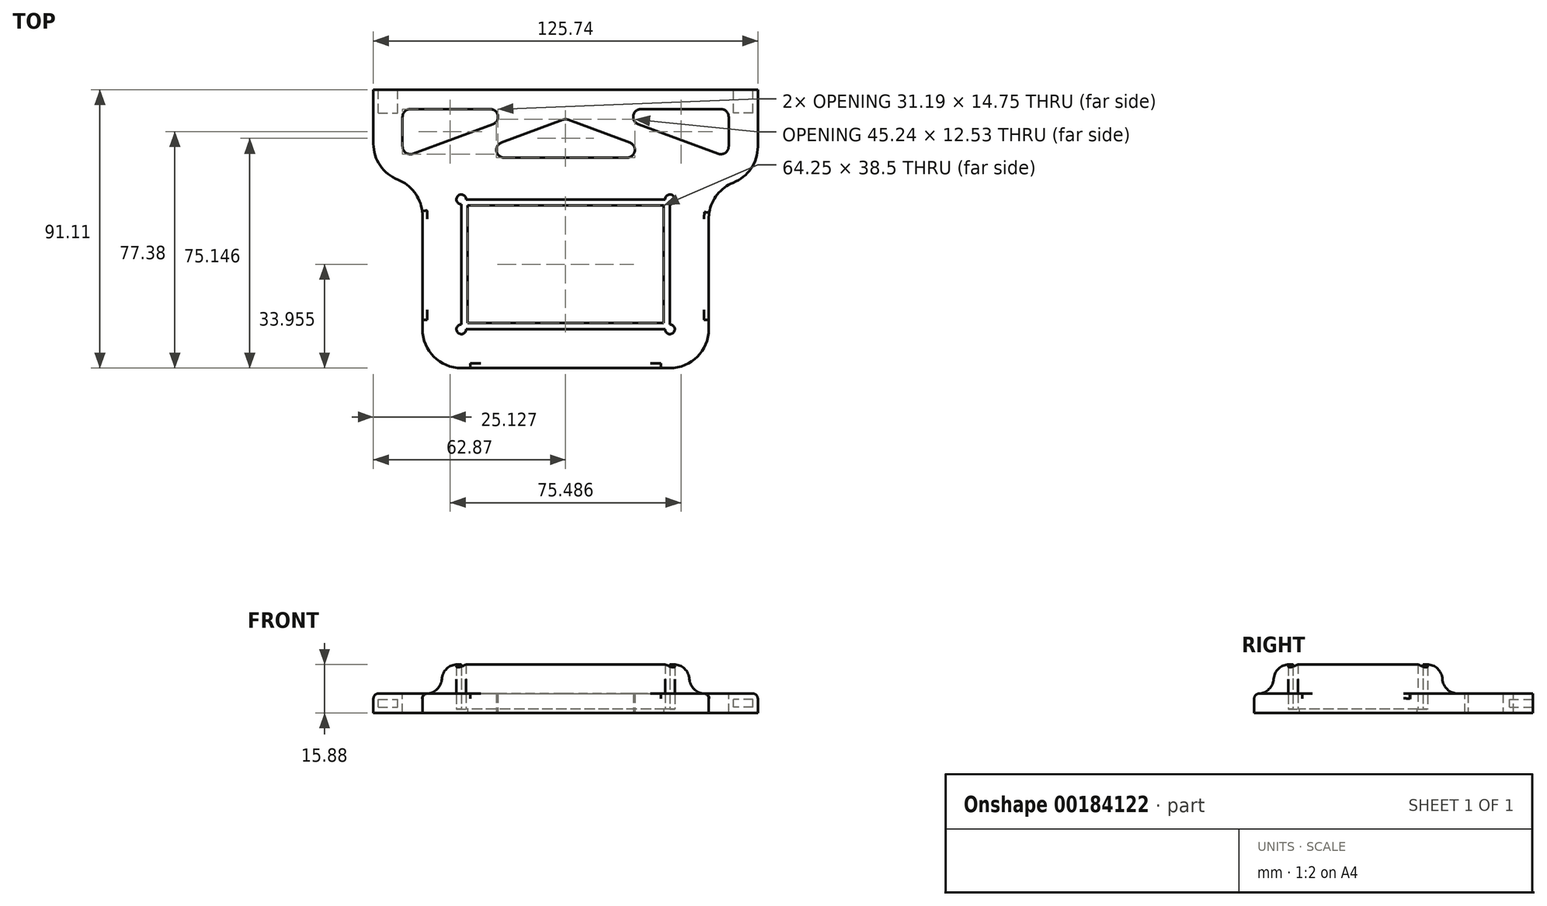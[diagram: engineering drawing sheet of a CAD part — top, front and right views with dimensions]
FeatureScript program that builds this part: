
annotation { "Feature Type Name" : "Feature", "Feature Type Description" : "" }
export const myFeature = defineFeature(function(context is Context, id is Id, definition is map)
    precondition{}
    {
        {
            var Q0;
            Q0=qCreatedBy(makeId("Top.planeOp"),FACE);
            var sketch = newSketch(context, id + "F0", { "sketchPlane" : qUnion([Q0])});
            skLineSegment(sketch, "E0", {"start": v(-53.34, 0) * mm, "end": v(-53.34, 47.62) * mm});
            skLineSegment(sketch, "E1", {"start": v(53.34, 0) * mm, "end": v(53.34, 47.62) * mm});
            skLineSegment(sketch, "E2", {"start": v(-39.21, 76.2) * mm, "end": v(39.21, 76.2) * mm});
            skArc(sketch, "E3", {"start": v(-39.21, 76.2) * mm, "mid": v(-55.15, 66.3) * mm, "end": v(-53.34, 47.62) * mm});
            skArc(sketch, "E4", {"start": v(53.34, 47.62) * mm, "mid": v(55.15, 66.3) * mm, "end": v(39.21, 76.2) * mm});
            skPoint(sketch, "E5", {"position": v(0, 76.2) * mm});
            skLineSegment(sketch, "E6.bottom", {"start": v(-58.42, 0) * mm, "end": v(58.42, 0) * mm, "construction": true});
            skLineSegment(sketch, "E6.top", {"start": v(-58.42, -82.55) * mm, "end": v(58.42, -82.55) * mm, "construction": true});
            skLineSegment(sketch, "E6.left", {"start": v(-58.42, 0) * mm, "end": v(-58.42, -82.55) * mm, "construction": true});
            skLineSegment(sketch, "E6.right", {"start": v(58.42, 0) * mm, "end": v(58.42, -82.55) * mm, "construction": true});
            skLineSegment(sketch, "E7.bottom", {"start": v(34.12, -20.03) * mm, "end": v(-34.12, -20.03) * mm});
            skLineSegment(sketch, "E7.top", {"start": v(34.13, -62.53) * mm, "end": v(-34.12, -62.53) * mm});
            skLineSegment(sketch, "E7.left", {"start": v(34.12, -20.03) * mm, "end": v(34.12, -62.52) * mm});
            skLineSegment(sketch, "E7.right", {"start": v(-34.12, -20.02) * mm, "end": v(-34.12, -62.53) * mm});
            skPoint(sketch, "E7.middle", {"position": v(0, -41.27) * mm});
            skPoint(sketch, "E8", {"position": v(58.42, -41.27) * mm});
            skCircle(sketch, "E9", {"center": v(-34.12, -20.02) * mm, "radius": 1.59 * mm});
            skCircle(sketch, "E10", {"center": v(34.13, -20.03) * mm, "radius": 1.59 * mm});
            skCircle(sketch, "E11", {"center": v(34.13, -62.52) * mm, "radius": 1.59 * mm});
            skCircle(sketch, "E12", {"center": v(-34.12, -62.53) * mm, "radius": 1.59 * mm});
            skLineSegment(sketch, "E13.0", {"start": v(-62.87, 0) * mm, "end": v(-62.87, 44.78) * mm});
            skLineSegment(sketch, "E13.1", {"start": v(62.87, 0) * mm, "end": v(62.87, 44.78) * mm});
            skArc(sketch, "E13.2", {"start": v(62.87, 44.78) * mm, "mid": v(62.86, 72.08) * mm, "end": v(39.21, 85.72) * mm});
            skLineSegment(sketch, "E13.3", {"start": v(-39.21, 85.73) * mm, "end": v(39.21, 85.73) * mm});
            skArc(sketch, "E13.4", {"start": v(-39.21, 85.72) * mm, "mid": v(-62.86, 72.08) * mm, "end": v(-62.87, 44.78) * mm});
            skLineSegment(sketch, "E14", {"start": v(-62.87, 0) * mm, "end": v(-53.34, 0) * mm});
            skLineSegment(sketch, "E15", {"start": v(53.34, 0) * mm, "end": v(62.87, 0) * mm});
            skLineSegment(sketch, "E16", {"start": v(-53.34, 15.88) * mm, "end": v(53.34, 15.88) * mm});
            skLineSegment(sketch, "E17", {"start": v(62.87, 0) * mm, "end": v(62.87, -91.27) * mm});
            skLineSegment(sketch, "E18", {"start": v(62.86, -91.27) * mm, "end": v(-62.86, -91.27) * mm});
            skLineSegment(sketch, "E19", {"start": v(-62.87, -91.27) * mm, "end": v(-62.87, 0) * mm});
            skLineSegment(sketch, "E20", {"start": v(0, -91.27) * mm, "end": v(0, -62.53) * mm, "construction": true});
            skLineSegment(sketch, "E21", {"start": v(34.12, -41.28) * mm, "end": v(62.87, -41.28) * mm, "construction": true});
            skLineSegment(sketch, "E22.bottom", {"start": v(40.48, -13.67) * mm, "end": v(-40.48, -13.67) * mm});
            skLineSegment(sketch, "E22.top", {"start": v(40.48, -68.88) * mm, "end": v(-40.48, -68.88) * mm});
            skLineSegment(sketch, "E22.left", {"start": v(40.48, -13.67) * mm, "end": v(40.48, -68.88) * mm});
            skLineSegment(sketch, "E22.right", {"start": v(-40.48, -13.67) * mm, "end": v(-40.48, -68.88) * mm});
            skLineSegment(sketch, "E23", {"start": v(-62.87, 0) * mm, "end": v(-62.87, -12.7) * mm});
            skLineSegment(sketch, "E24", {"start": v(-62.87, -12.7) * mm, "end": v(-46.83, -12.7) * mm});
            skLineSegment(sketch, "E25", {"start": v(-46.83, -12.7) * mm, "end": v(-46.83, -75.22) * mm});
            skLineSegment(sketch, "E26", {"start": v(-46.83, -75.22) * mm, "end": v(46.83, -75.22) * mm});
            skLineSegment(sketch, "E27", {"start": v(46.83, -75.22) * mm, "end": v(46.83, -13.67) * mm});
            skLineSegment(sketch, "E28", {"start": v(46.83, -13.67) * mm, "end": v(62.87, -13.67) * mm});
            skLineSegment(sketch, "E29", {"start": v(62.87, -13.67) * mm, "end": v(62.87, 0) * mm});
            skLineSegment(sketch, "E30", {"start": v(-53.34, 15.88) * mm, "end": v(-62.87, 15.88) * mm});
            skLineSegment(sketch, "E31", {"start": v(53.34, 15.88) * mm, "end": v(62.87, 15.88) * mm});
            skSolve(sketch);
        }
        {
            var Q0;
            {var subQ16=sQuery(id+"F0.wireOp",EDGE,"E14");Q0=makeQuery(id+"F0.imprint","IMPRINT",FACE,{"disambiguationData":[TD([[makeQuery(id+"F0.imprint","IMPRINT",EDGE,{"derivedFrom":subQ16}),-1.0]])]});}
            var Q1;
            Q1=makeQuery(id+"F0.imprint","IMPRINT",FACE,{"disambiguationData":[TD([[makeQuery(id+"F0.imprint","IMPRINT",EDGE,{"derivedFrom":sQuery(id+"F0.wireOp",EDGE,"E22.bottom")}),1.0]])]});
            var Q2;
            {var subQ0=sQuery(id+"F0.wireOp",EDGE,"E14");Q2=makeQuery(id+"F0.imprint","IMPRINT",FACE,{"disambiguationData":[TD([[makeQuery(id+"F0.imprint","IMPRINT",EDGE,{"derivedFrom":subQ0}),1.0]])]});}
            var Q3;
            {var subQ0=sQuery(id+"F0.wireOp",EDGE,"E15");Q3=makeQuery(id+"F0.imprint","IMPRINT",FACE,{"disambiguationData":[TD([[makeQuery(id+"F0.imprint","IMPRINT",EDGE,{"derivedFrom":subQ0}),1.0]])]});}
            extrude(context, id + "F1", {"entities" : qUnion([Q0, Q1, Q2, Q3]), "depth" : 6.35 * mm});
        }
        {
            var Q0;
            Q0=makeQuery(id+"F0.imprint","IMPRINT",FACE,{"disambiguationData":[TD([[makeQuery(id+"F0.imprint","IMPRINT",EDGE,{"derivedFrom":sQuery(id+"F0.wireOp",EDGE,"E22.bottom")}),1.0]])]});
            extrude(context, id + "F2", {"entities" : qUnion([Q0]), "operationType" : NewBodyOperationType.ADD, "depth" : 15.88 * mm});
        }
        {
            var Q0;
            Q0=makeQuery(id+"F1.opExtrude","CAP_FACE",FACE,{"disambiguationData":[OSD([sQuery(id+"F0.wireOp",EDGE,"E7.bottom"),sQuery(id+"F0.wireOp",EDGE,"E7.top"),sQuery(id+"F0.wireOp",EDGE,"E7.left"),sQuery(id+"F0.wireOp",EDGE,"E7.right"),sQuery(id+"F0.wireOp",EDGE,"E9"),sQuery(id+"F0.wireOp",EDGE,"E10"),sQuery(id+"F0.wireOp",EDGE,"E11"),sQuery(id+"F0.wireOp",EDGE,"E12"),sQuery(id+"F0.wireOp",EDGE,"E13.0"),sQuery(id+"F0.wireOp",EDGE,"E13.1"),sQuery(id+"F0.wireOp",EDGE,"E16"),sQuery(id+"F0.wireOp",EDGE,"E23"),sQuery(id+"F0.wireOp",EDGE,"E24"),sQuery(id+"F0.wireOp",EDGE,"E25"),sQuery(id+"F0.wireOp",EDGE,"E26"),sQuery(id+"F0.wireOp",EDGE,"E27"),sQuery(id+"F0.wireOp",EDGE,"E28"),sQuery(id+"F0.wireOp",EDGE,"E29"),sQuery(id+"F0.wireOp",EDGE,"E30"),sQuery(id+"F0.wireOp",EDGE,"E31")])],"isStart":false});
            var sketch = newSketch(context, id + "F3", { "sketchPlane" : qUnion([Q0])});
            skLineSegment(sketch, "E32", {"start": v(-53.34, 9.52) * mm, "end": v(-53.34, -6.35) * mm});
            skLineSegment(sketch, "E33", {"start": v(-53.34, -6.35) * mm, "end": v(-10.48, 9.53) * mm});
            skLineSegment(sketch, "E34", {"start": v(-10.48, 9.53) * mm, "end": v(-53.34, 9.52) * mm});
            skLineSegment(sketch, "E35", {"start": v(10.48, 9.53) * mm, "end": v(53.34, 9.53) * mm});
            skLineSegment(sketch, "E36", {"start": v(53.34, 9.52) * mm, "end": v(53.34, -6.35) * mm});
            skLineSegment(sketch, "E37", {"start": v(53.34, -6.35) * mm, "end": v(10.48, 9.53) * mm});
            skLineSegment(sketch, "E38", {"start": v(0, 6.35) * mm, "end": v(-34.3, -6.35) * mm});
            skLineSegment(sketch, "E39", {"start": v(-34.3, -6.35) * mm, "end": v(34.3, -6.35) * mm});
            skLineSegment(sketch, "E40", {"start": v(34.3, -6.35) * mm, "end": v(0, 6.35) * mm});
            skLineSegment(sketch, "E41", {"start": v(-10.48, 9.53) * mm, "end": v(10.48, 9.53) * mm, "construction": true});
            skPoint(sketch, "E42", {"position": v(0, 9.53) * mm});
            skPoint(sketch, "E43", {"position": v(-53.34, 1.59) * mm});
            skPoint(sketch, "E44", {"position": v(-62.87, 1.59) * mm});
            skSolve(sketch);
        }
        {
            var Q0;
            Q0 = qSketchRegion(id + "F3", true);
            extrude(context, id + "F4", {"entities" : qUnion([Q0]), "operationType" : NewBodyOperationType.REMOVE, "endBound" : BoundingType.THROUGH_ALL, "oppositeDirection" : true, "depth" : 25.4 * mm});
        }
        {
            var Q0;
            Q0=makeQuery(id+"F1.opExtrude","SWEPT_EDGE",EDGE,{"disambiguationData":[OSD([sQuery(id+"F0.wireOp",EDGE,"E25"),sQuery(id+"F0.wireOp",EDGE,"E26")])]});
            var Q1;
            Q1=makeQuery(id+"F1.opExtrude","SWEPT_EDGE",EDGE,{"disambiguationData":[OSD([sQuery(id+"F0.wireOp",EDGE,"E26"),sQuery(id+"F0.wireOp",EDGE,"E27")])]});
            var Q2;
            Q2=makeQuery(id+"F1.opExtrude","SWEPT_EDGE",EDGE,{"disambiguationData":[OSD([sQuery(id+"F0.wireOp",EDGE,"E24"),sQuery(id+"F0.wireOp",EDGE,"E25")])]});
            var Q3;
            Q3=makeQuery(id+"F1.opExtrude","SWEPT_EDGE",EDGE,{"disambiguationData":[OSD([sQuery(id+"F0.wireOp",EDGE,"E27"),sQuery(id+"F0.wireOp",EDGE,"E28")])]});
            var Q4;
            Q4=makeQuery(id+"F2.opExtrude","SWEPT_EDGE",EDGE,{"disambiguationData":[OSD([sQuery(id+"F0.wireOp",EDGE,"E22.top"),sQuery(id+"F0.wireOp",EDGE,"E22.left")])]});
            var Q5;
            Q5=makeQuery(id+"F2.opExtrude","SWEPT_EDGE",EDGE,{"disambiguationData":[OSD([sQuery(id+"F0.wireOp",EDGE,"E22.top"),sQuery(id+"F0.wireOp",EDGE,"E22.right")])]});
            var Q6;
            Q6=makeQuery(id+"F2.opExtrude","SWEPT_EDGE",EDGE,{"disambiguationData":[OSD([sQuery(id+"F0.wireOp",EDGE,"E22.bottom"),sQuery(id+"F0.wireOp",EDGE,"E22.left")])]});
            var Q7;
            Q7=makeQuery(id+"F2.opExtrude","SWEPT_EDGE",EDGE,{"disambiguationData":[OSD([sQuery(id+"F0.wireOp",EDGE,"E22.bottom"),sQuery(id+"F0.wireOp",EDGE,"E22.right")])]});
            fillet(context, id + "F5", {"entities" : qUnion([Q0, Q1, Q2, Q3, Q4, Q5, Q6, Q7]), "radius" : 12.7 * mm, "tangentPropagation" : true, "allowEdgeOverflow" : false});
        }
        {
            var Q0;
            Q0=makeQuery(id+"F1.opExtrude","SWEPT_EDGE",EDGE,{"disambiguationData":[OSD([sQuery(id+"F0.wireOp",EDGE,"E19"),sQuery(id+"F0.wireOp",EDGE,"E23"),sQuery(id+"F0.wireOp",EDGE,"E24")])]});
            var Q1;
            Q1=makeQuery(id+"F1.opExtrude","SWEPT_EDGE",EDGE,{"disambiguationData":[OSD([sQuery(id+"F0.wireOp",EDGE,"E17"),sQuery(id+"F0.wireOp",EDGE,"E28"),sQuery(id+"F0.wireOp",EDGE,"E29")])]});
            fillet(context, id + "F6", {"entities" : qUnion([Q0, Q1]), "radius" : 12.7 * mm, "tangentPropagation" : true, "allowEdgeOverflow" : false});
        }
        {
            var Q0;
            Q0=makeQuery(id+"F5.opFillet","BLEND_EDGE",EDGE,{"blendedFrom":[makeQuery(id+"F2.opExtrude","SWEPT_EDGE",EDGE,{"disambiguationData":[OSD([sQuery(id+"F0.wireOp",EDGE,"E22.bottom"),sQuery(id+"F0.wireOp",EDGE,"E22.left")])]}),makeQuery(id+"F1.opExtrude","CAP_FACE",FACE,{"disambiguationData":[OSD([sQuery(id+"F0.wireOp",EDGE,"E7.bottom"),sQuery(id+"F0.wireOp",EDGE,"E7.top"),sQuery(id+"F0.wireOp",EDGE,"E7.left"),sQuery(id+"F0.wireOp",EDGE,"E7.right"),sQuery(id+"F0.wireOp",EDGE,"E9"),sQuery(id+"F0.wireOp",EDGE,"E10"),sQuery(id+"F0.wireOp",EDGE,"E11"),sQuery(id+"F0.wireOp",EDGE,"E12"),sQuery(id+"F0.wireOp",EDGE,"E13.0"),sQuery(id+"F0.wireOp",EDGE,"E13.1"),sQuery(id+"F0.wireOp",EDGE,"E16"),sQuery(id+"F0.wireOp",EDGE,"E23"),sQuery(id+"F0.wireOp",EDGE,"E24"),sQuery(id+"F0.wireOp",EDGE,"E25"),sQuery(id+"F0.wireOp",EDGE,"E26"),sQuery(id+"F0.wireOp",EDGE,"E27"),sQuery(id+"F0.wireOp",EDGE,"E28"),sQuery(id+"F0.wireOp",EDGE,"E29"),sQuery(id+"F0.wireOp",EDGE,"E30"),sQuery(id+"F0.wireOp",EDGE,"E31")])],"isStart":false})],"blendedInto":[makeQuery(id+"F1.opExtrude","CAP_FACE",FACE,{"disambiguationData":[OSD([sQuery(id+"F0.wireOp",EDGE,"E7.bottom"),sQuery(id+"F0.wireOp",EDGE,"E7.top"),sQuery(id+"F0.wireOp",EDGE,"E7.left"),sQuery(id+"F0.wireOp",EDGE,"E7.right"),sQuery(id+"F0.wireOp",EDGE,"E9"),sQuery(id+"F0.wireOp",EDGE,"E10"),sQuery(id+"F0.wireOp",EDGE,"E11"),sQuery(id+"F0.wireOp",EDGE,"E12"),sQuery(id+"F0.wireOp",EDGE,"E13.0"),sQuery(id+"F0.wireOp",EDGE,"E13.1"),sQuery(id+"F0.wireOp",EDGE,"E16"),sQuery(id+"F0.wireOp",EDGE,"E23"),sQuery(id+"F0.wireOp",EDGE,"E24"),sQuery(id+"F0.wireOp",EDGE,"E25"),sQuery(id+"F0.wireOp",EDGE,"E26"),sQuery(id+"F0.wireOp",EDGE,"E27"),sQuery(id+"F0.wireOp",EDGE,"E28"),sQuery(id+"F0.wireOp",EDGE,"E29"),sQuery(id+"F0.wireOp",EDGE,"E30"),sQuery(id+"F0.wireOp",EDGE,"E31")])],"isStart":false})]});
            fillet(context, id + "F7", {"entities" : qUnion([Q0]), "radius" : 5.08 * mm, "tangentPropagation" : true, "allowEdgeOverflow" : false});
        }
        {
            var Q0;
            Q0=makeQuery(id+"F4.boolean.opBoolean","COPY",EDGE,{"derivedFrom":makeQuery(id+"F4.opExtrude","SWEPT_EDGE",EDGE,{"disambiguationData":[OSD([sQuery(id+"F3.wireOp",EDGE,"E32"),sQuery(id+"F3.wireOp",EDGE,"E34")])]})});
            var Q1;
            Q1=makeQuery(id+"F4.boolean.opBoolean","COPY",EDGE,{"derivedFrom":makeQuery(id+"F4.opExtrude","SWEPT_EDGE",EDGE,{"disambiguationData":[OSD([sQuery(id+"F3.wireOp",EDGE,"E32"),sQuery(id+"F3.wireOp",EDGE,"E33")])]})});
            var Q2;
            Q2=makeQuery(id+"F4.boolean.opBoolean","COPY",EDGE,{"derivedFrom":makeQuery(id+"F4.opExtrude","SWEPT_EDGE",EDGE,{"disambiguationData":[OSD([sQuery(id+"F3.wireOp",EDGE,"E36"),sQuery(id+"F3.wireOp",EDGE,"E37")])]})});
            var Q3;
            Q3=makeQuery(id+"F4.boolean.opBoolean","COPY",EDGE,{"derivedFrom":makeQuery(id+"F4.opExtrude","SWEPT_EDGE",EDGE,{"disambiguationData":[OSD([sQuery(id+"F3.wireOp",EDGE,"E35"),sQuery(id+"F3.wireOp",EDGE,"E37")])]})});
            var Q4;
            Q4=makeQuery(id+"F4.boolean.opBoolean","COPY",EDGE,{"derivedFrom":makeQuery(id+"F4.opExtrude","SWEPT_EDGE",EDGE,{"disambiguationData":[OSD([sQuery(id+"F3.wireOp",EDGE,"E38"),sQuery(id+"F3.wireOp",EDGE,"E40")])]})});
            var Q5;
            Q5=makeQuery(id+"F4.boolean.opBoolean","COPY",EDGE,{"derivedFrom":makeQuery(id+"F4.opExtrude","SWEPT_EDGE",EDGE,{"disambiguationData":[OSD([sQuery(id+"F3.wireOp",EDGE,"E39"),sQuery(id+"F3.wireOp",EDGE,"E40")])]})});
            var Q6;
            Q6=makeQuery(id+"F4.boolean.opBoolean","COPY",EDGE,{"derivedFrom":makeQuery(id+"F4.opExtrude","SWEPT_EDGE",EDGE,{"disambiguationData":[OSD([sQuery(id+"F3.wireOp",EDGE,"E38"),sQuery(id+"F3.wireOp",EDGE,"E39")])]})});
            var Q7;
            Q7=makeQuery(id+"F4.boolean.opBoolean","COPY",EDGE,{"derivedFrom":makeQuery(id+"F4.opExtrude","SWEPT_EDGE",EDGE,{"disambiguationData":[OSD([sQuery(id+"F3.wireOp",EDGE,"E33"),sQuery(id+"F3.wireOp",EDGE,"E34")])]})});
            var Q8;
            Q8=makeQuery(id+"F4.boolean.opBoolean","COPY",EDGE,{"derivedFrom":makeQuery(id+"F4.opExtrude","SWEPT_EDGE",EDGE,{"disambiguationData":[OSD([sQuery(id+"F3.wireOp",EDGE,"E35"),sQuery(id+"F3.wireOp",EDGE,"E36")])]})});
            fillet(context, id + "F8", {"entities" : qUnion([Q0, Q1, Q2, Q3, Q4, Q5, Q6, Q7, Q8]), "radius" : 2.54 * mm, "tangentPropagation" : true, "allowEdgeOverflow" : false});
        }
        {
            var Q0;
            Q0=makeQuery(id+"F1.opExtrude","SWEPT_FACE",FACE,{"disambiguationData":[OSD([sQuery(id+"F0.wireOp",EDGE,"E16"),sQuery(id+"F0.wireOp",EDGE,"E30"),sQuery(id+"F0.wireOp",EDGE,"E31")])]});
            var sketch = newSketch(context, id + "F9", { "sketchPlane" : qUnion([Q0])});
            skLineSegment(sketch, "E45.bottom", {"start": v(61.28, 1.9) * mm, "end": v(54.93, 1.9) * mm});
            skLineSegment(sketch, "E45.top", {"start": v(61.28, 4.44) * mm, "end": v(54.93, 4.44) * mm});
            skLineSegment(sketch, "E45.left", {"start": v(61.28, 1.9) * mm, "end": v(61.28, 4.44) * mm});
            skLineSegment(sketch, "E45.right", {"start": v(54.93, 1.9) * mm, "end": v(54.93, 4.44) * mm});
            skPoint(sketch, "E45.middle", {"position": v(58.1, 3.17) * mm});
            skLineSegment(sketch, "E46.bottom", {"start": v(-61.28, 1.9) * mm, "end": v(-54.93, 1.9) * mm});
            skLineSegment(sketch, "E46.top", {"start": v(-61.28, 4.44) * mm, "end": v(-54.93, 4.44) * mm});
            skLineSegment(sketch, "E46.left", {"start": v(-61.28, 1.9) * mm, "end": v(-61.28, 4.44) * mm});
            skLineSegment(sketch, "E46.right", {"start": v(-54.93, 1.9) * mm, "end": v(-54.93, 4.44) * mm});
            skPoint(sketch, "E46.middle", {"position": v(-58.1, 3.17) * mm});
            skLineSegment(sketch, "E47", {"start": v(0, 0) * mm, "end": v(0, 6.35) * mm, "construction": true});
            skPoint(sketch, "E48", {"position": v(0, 3.17) * mm});
            skLineSegment(sketch, "E49", {"start": v(-58.1, 3.17) * mm, "end": v(58.1, 3.18) * mm, "construction": true});
            skLineSegment(sketch, "E50", {"start": v(-62.87, 6.35) * mm, "end": v(-62.87, 3.17) * mm, "construction": true});
            skLineSegment(sketch, "E51", {"start": v(-62.87, 3.17) * mm, "end": v(-62.87, 0) * mm, "construction": true});
            skSolve(sketch);
        }
        {
            var Q0;
            Q0 = qSketchRegion(id + "F9", true);
            extrude(context, id + "F10", {"entities" : qUnion([Q0]), "operationType" : NewBodyOperationType.REMOVE, "oppositeDirection" : true, "depth" : 7.62 * mm});
        }
        {
            var Q0;
            {var subQ1=sQuery(id+"F0.wireOp",EDGE,"E14");Q0=makeQuery(id+"F0.imprint","IMPRINT",FACE,{"disambiguationData":[TD([[makeQuery(id+"F0.imprint","IMPRINT",EDGE,{"derivedFrom":subQ1}),-1.0]])]});}
            var sketch = newSketch(context, id + "F11", { "sketchPlane" : qUnion([Q0])});
            skLineSegment(sketch, "E52.bottom", {"start": v(32.13, -22.03) * mm, "end": v(-32.12, -22.03) * mm});
            skLineSegment(sketch, "E52.top", {"start": v(32.13, -60.53) * mm, "end": v(-32.12, -60.53) * mm});
            skLineSegment(sketch, "E52.left", {"start": v(32.13, -22.03) * mm, "end": v(32.13, -60.53) * mm});
            skLineSegment(sketch, "E52.right", {"start": v(-32.12, -22.03) * mm, "end": v(-32.12, -60.53) * mm});
            skPoint(sketch, "E52.middle", {"position": v(0, -41.28) * mm});
            skLineSegment(sketch, "E53.bottom", {"start": v(35.71, -18.44) * mm, "end": v(-35.71, -18.44) * mm});
            skLineSegment(sketch, "E53.top", {"start": v(35.71, -64.11) * mm, "end": v(-35.71, -64.11) * mm});
            skLineSegment(sketch, "E53.left", {"start": v(35.71, -18.44) * mm, "end": v(35.71, -64.11) * mm});
            skLineSegment(sketch, "E53.right", {"start": v(-35.71, -18.44) * mm, "end": v(-35.71, -64.11) * mm});
            skSolve(sketch);
        }
        {
            var Q0;
            Q0=makeQuery(id+"F0.imprint","IMPRINT",FACE,{"disambiguationData":[TD([[makeQuery(id+"F0.imprint","IMPRINT",EDGE,{"derivedFrom":sQuery(id+"F0.wireOp",EDGE,"E22.bottom")}),1.0]])]});
            var Q1;
            Q1=makeQuery(id+"F11.imprint","IMPRINT",FACE,{"disambiguationData":[TD([[makeQuery(id+"F11.imprint","IMPRINT",EDGE,{"derivedFrom":sQuery(id+"F11.wireOp",EDGE,"E52.bottom")}),-1.0]])]});
            extrude(context, id + "F12", {"entities" : qUnion([Q0, Q1]), "operationType" : NewBodyOperationType.ADD, "depth" : 1.27 * mm});
        }
        {
            var Q0;
            {var subQ0=sQuery(id+"F0.wireOp",EDGE,"E29");var subQ1=sQuery(id+"F0.wireOp",EDGE,"E28");Q0=makeQuery(id+"F6.opFillet","BLEND_EDGE",EDGE,{"blendedFrom":[makeQuery(id+"F1.opExtrude","SWEPT_EDGE",EDGE,{"disambiguationData":[OSD([sQuery(id+"F0.wireOp",EDGE,"E17"),subQ1,subQ0])]}),makeQuery(id+"F1.opExtrude","CAP_FACE",FACE,{"disambiguationData":[OSD([sQuery(id+"F0.wireOp",EDGE,"E7.bottom"),sQuery(id+"F0.wireOp",EDGE,"E7.top"),sQuery(id+"F0.wireOp",EDGE,"E7.left"),sQuery(id+"F0.wireOp",EDGE,"E7.right"),sQuery(id+"F0.wireOp",EDGE,"E9"),sQuery(id+"F0.wireOp",EDGE,"E10"),sQuery(id+"F0.wireOp",EDGE,"E11"),sQuery(id+"F0.wireOp",EDGE,"E12"),sQuery(id+"F0.wireOp",EDGE,"E13.0"),sQuery(id+"F0.wireOp",EDGE,"E13.1"),sQuery(id+"F0.wireOp",EDGE,"E16"),sQuery(id+"F0.wireOp",EDGE,"E23"),sQuery(id+"F0.wireOp",EDGE,"E24"),sQuery(id+"F0.wireOp",EDGE,"E25"),sQuery(id+"F0.wireOp",EDGE,"E26"),sQuery(id+"F0.wireOp",EDGE,"E27"),subQ1,subQ0,sQuery(id+"F0.wireOp",EDGE,"E30"),sQuery(id+"F0.wireOp",EDGE,"E31")])],"isStart":false})],"blendedInto":[makeQuery(id+"F1.opExtrude","CAP_FACE",FACE,{"disambiguationData":[OSD([sQuery(id+"F0.wireOp",EDGE,"E7.bottom"),sQuery(id+"F0.wireOp",EDGE,"E7.top"),sQuery(id+"F0.wireOp",EDGE,"E7.left"),sQuery(id+"F0.wireOp",EDGE,"E7.right"),sQuery(id+"F0.wireOp",EDGE,"E9"),sQuery(id+"F0.wireOp",EDGE,"E10"),sQuery(id+"F0.wireOp",EDGE,"E11"),sQuery(id+"F0.wireOp",EDGE,"E12"),sQuery(id+"F0.wireOp",EDGE,"E13.0"),sQuery(id+"F0.wireOp",EDGE,"E13.1"),sQuery(id+"F0.wireOp",EDGE,"E16"),sQuery(id+"F0.wireOp",EDGE,"E23"),sQuery(id+"F0.wireOp",EDGE,"E24"),sQuery(id+"F0.wireOp",EDGE,"E25"),sQuery(id+"F0.wireOp",EDGE,"E26"),sQuery(id+"F0.wireOp",EDGE,"E27"),subQ1,subQ0,sQuery(id+"F0.wireOp",EDGE,"E30"),sQuery(id+"F0.wireOp",EDGE,"E31")])],"isStart":false})]});}
            fillet(context, id + "F13", {"entities" : qUnion([Q0]), "radius" : 1.59 * mm, "tangentPropagation" : true, "allowEdgeOverflow" : false});
        }
        {
            var Q0;
            Q0=makeQuery(id+"F2.opExtrude","CAP_EDGE",EDGE,{"disambiguationData":[OSD([sQuery(id+"F0.wireOp",EDGE,"E22.bottom")])],"isStart":false});
            fillet(context, id + "F14", {"entities" : qUnion([Q0]), "radius" : 5.08 * mm, "tangentPropagation" : true, "allowEdgeOverflow" : false});
        }
    });
